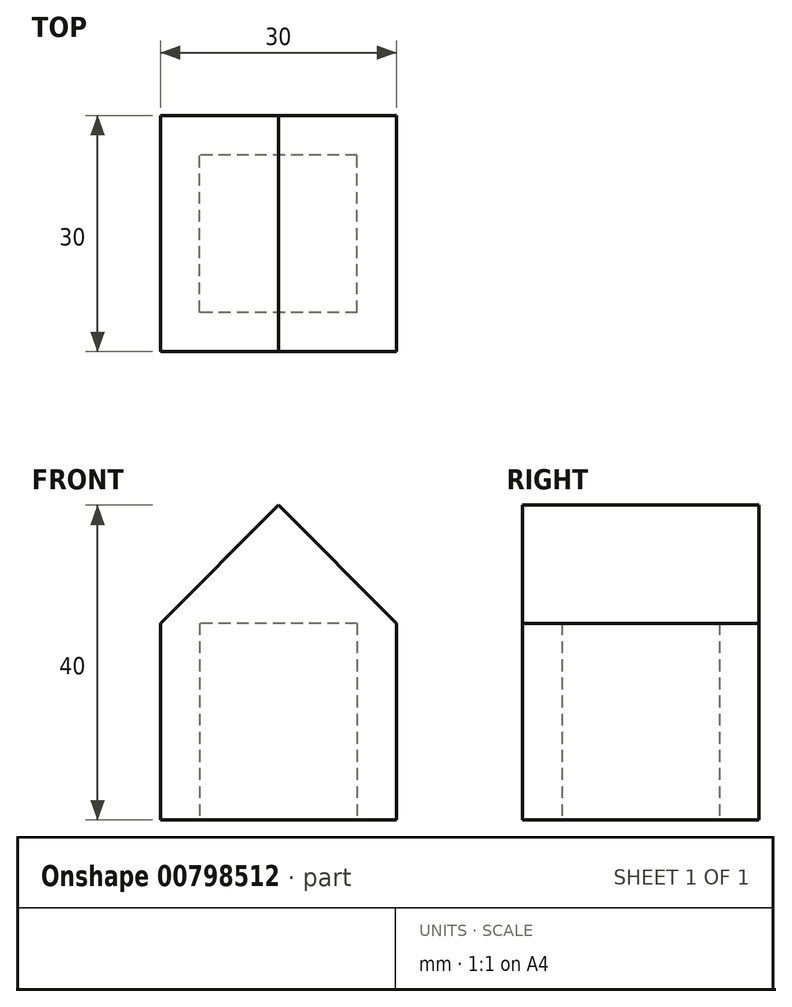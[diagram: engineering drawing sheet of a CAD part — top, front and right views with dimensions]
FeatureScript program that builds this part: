
annotation { "Feature Type Name" : "Feature", "Feature Type Description" : "" }
export const myFeature = defineFeature(function(context is Context, id is Id, definition is map)
    precondition{}
    {
        {
            var Q0;
            Q0=qCreatedBy(makeId("Top.planeOp"),FACE);
            var sketch = newSketch(context, id + "F0", { "sketchPlane" : qUnion([Q0])});
            skLineSegment(sketch, "E0.bottom", {"start": v(0, 30) * mm, "end": v(30, 30) * mm});
            skLineSegment(sketch, "E0.top", {"start": v(0, 0) * mm, "end": v(30, 0) * mm});
            skLineSegment(sketch, "E0.left", {"start": v(0, 30) * mm, "end": v(0, 0) * mm});
            skLineSegment(sketch, "E0.right", {"start": v(30, 30) * mm, "end": v(30, 0) * mm});
            skLineSegment(sketch, "E1.bottom", {"start": v(25, 5) * mm, "end": v(5, 5) * mm});
            skLineSegment(sketch, "E1.top", {"start": v(25, 25) * mm, "end": v(5, 25) * mm});
            skLineSegment(sketch, "E1.left", {"start": v(25, 5) * mm, "end": v(25, 25) * mm});
            skLineSegment(sketch, "E1.right", {"start": v(5, 5) * mm, "end": v(5, 25) * mm});
            skPoint(sketch, "E1.middle", {"position": v(15, 15) * mm});
            skLineSegment(sketch, "E2", {"start": v(15, 15) * mm, "end": v(15, 30) * mm, "construction": true});
            skLineSegment(sketch, "E3", {"start": v(15, 15) * mm, "end": v(0, 15) * mm, "construction": true});
            skSolve(sketch);
        }
        {
            var Q0;
            Q0 = qSketchRegion(id + "F0", true);
            extrude(context, id + "F1", {"entities" : qUnion([Q0]), "depth" : 25 * mm, "offsetDistance" : 25 * mm});
        }
        {
            var Q0;
            Q0=makeQuery(id+"F1.opExtrude","CAP_FACE",FACE,{"disambiguationData":[OSD([sQuery(id+"F0.wireOp",EDGE,"E0.bottom"),sQuery(id+"F0.wireOp",EDGE,"E0.top"),sQuery(id+"F0.wireOp",EDGE,"E0.left"),sQuery(id+"F0.wireOp",EDGE,"E0.right"),sQuery(id+"F0.wireOp",EDGE,"E1.bottom"),sQuery(id+"F0.wireOp",EDGE,"E1.top"),sQuery(id+"F0.wireOp",EDGE,"E1.left"),sQuery(id+"F0.wireOp",EDGE,"E1.right")])],"isStart":false});
            var sketch = newSketch(context, id + "F2", { "sketchPlane" : qUnion([Q0])});
            skLineSegment(sketch, "E4.bottom", {"start": v(0, 30) * mm, "end": v(30, 30) * mm});
            skLineSegment(sketch, "E4.top", {"start": v(0, 0) * mm, "end": v(30, 0) * mm});
            skLineSegment(sketch, "E4.left", {"start": v(0, 30) * mm, "end": v(0, 0) * mm});
            skLineSegment(sketch, "E4.right", {"start": v(30, 30) * mm, "end": v(30, 0) * mm});
            skSolve(sketch);
        }
        {
            var Q0;
            Q0 = qSketchRegion(id + "F2", true);
            extrude(context, id + "F3", {"entities" : qUnion([Q0]), "operationType" : NewBodyOperationType.ADD, "depth" : 25 * mm, "offsetDistance" : 25 * mm});
        }
        {
            var Q0;
            Q0=makeQuery(id+"F3.opExtrude","CAP_EDGE",EDGE,{"disambiguationData":[OSD([sQuery(id+"F2.wireOp",EDGE,"E4.left")])],"isStart":false});
            var Q1;
            Q1=makeQuery(id+"F3.opExtrude","CAP_EDGE",EDGE,{"disambiguationData":[OSD([sQuery(id+"F2.wireOp",EDGE,"E4.right")])],"isStart":false});
            chamfer(context, id + "F4", {"entities" : qUnion([Q0, Q1]), "width" : 25 * mm, "tangentPropagation" : true});
        }
    });
